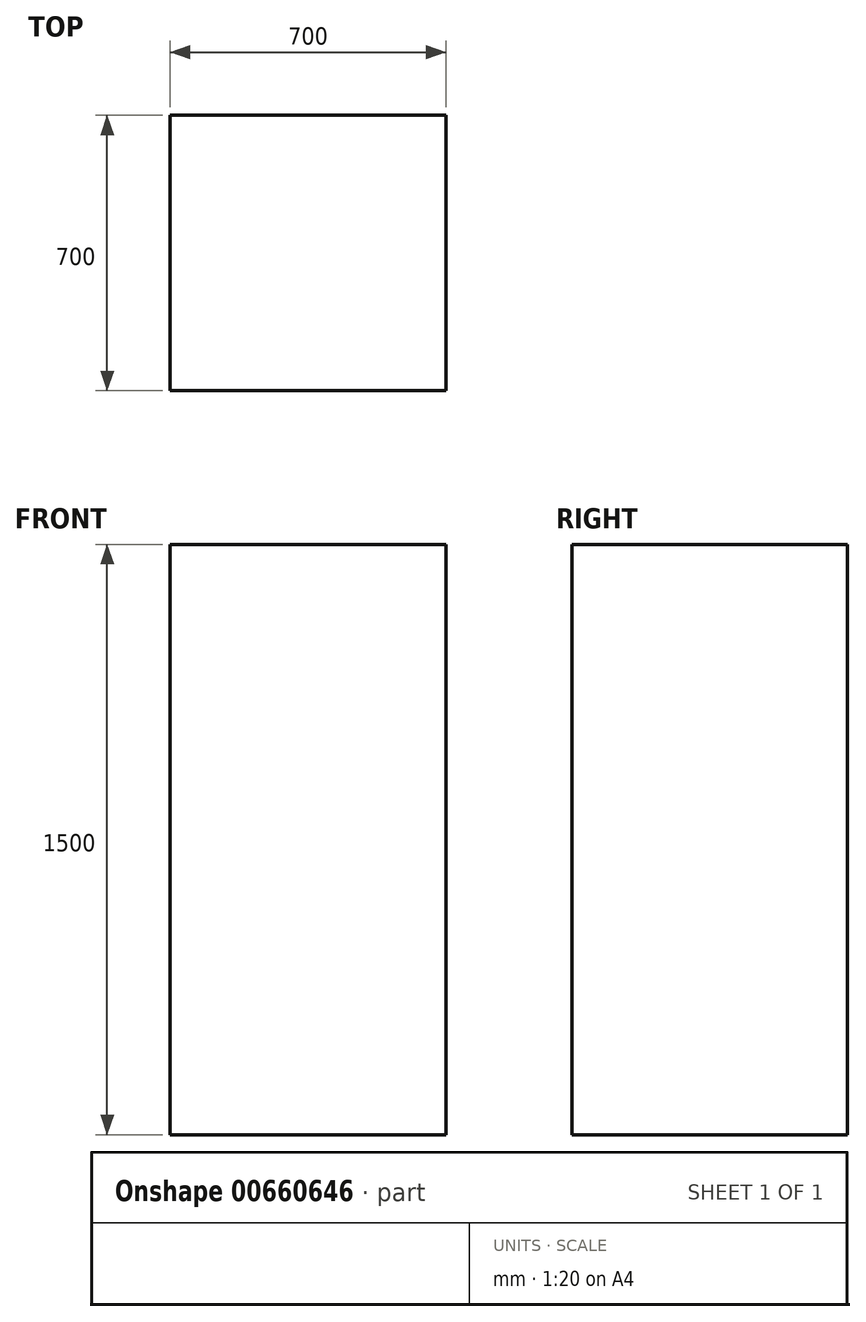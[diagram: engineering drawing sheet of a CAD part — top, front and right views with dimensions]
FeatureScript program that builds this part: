
annotation { "Feature Type Name" : "Feature", "Feature Type Description" : "" }
export const myFeature = defineFeature(function(context is Context, id is Id, definition is map)
    precondition{}
    {
        {
            var Q0;
            Q0=qCreatedBy(makeId("Top.planeOp"),FACE);
            var sketch = newSketch(context, id + "F0", { "sketchPlane" : qUnion([Q0])});
            skLineSegment(sketch, "E0.bottom", {"start": v(0, 28.24) * mm, "end": v(0, 28.24) * mm});
            skLineSegment(sketch, "E0.top", {"start": v(0, -28.24) * mm, "end": v(0, -28.24) * mm});
            skLineSegment(sketch, "E0.left", {"start": v(0, 28.24) * mm, "end": v(0, -28.24) * mm});
            skLineSegment(sketch, "E0.right", {"start": v(0, 28.24) * mm, "end": v(0, -28.24) * mm});
            skPoint(sketch, "E0.middle", {"position": v(0, 0) * mm});
            skLineSegment(sketch, "E1.bottom", {"start": v(350, 350) * mm, "end": v(-350, 350) * mm});
            skLineSegment(sketch, "E1.top", {"start": v(350, -350) * mm, "end": v(-350, -350) * mm});
            skLineSegment(sketch, "E1.left", {"start": v(350, 350) * mm, "end": v(350, -350) * mm});
            skLineSegment(sketch, "E1.right", {"start": v(-350, 350) * mm, "end": v(-350, -350) * mm});
            skSolve(sketch);
        }
        {
            var Q0;
            Q0=makeQuery(id+"F0.imprint","IMPRINT",FACE,{"disambiguationData":[TD([[makeQuery(id+"F0.imprint","IMPRINT",EDGE,{"derivedFrom":sQuery(id+"F0.wireOp",EDGE,"E1.bottom")}),1.0]])]});
            extrude(context, id + "F1", {"entities" : qUnion([Q0]), "depth" : 1500 * mm, "offsetDistance" : 25 * mm});
        }
    });
